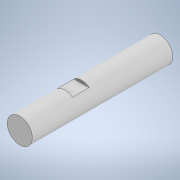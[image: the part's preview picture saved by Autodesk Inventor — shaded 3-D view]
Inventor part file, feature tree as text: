
AUTODESK INVENTOR PART (.ipt)
format: ipt  version: 2021 (Build 250183000, 183)  size: 99,840 bytes
history: native  units: in
note: dims shown in document units (in); Inventor stores cm internally (conversion verified against a paired STEP export)
features: extrude x2, sketch x2, other x1, plane x1
ambient origin geometry x8: Origin, YZ Plane, XZ Plane, XY Plane, X Axis, Y Axis, Z Axis, Center Point
bodies: Body1 (feature_tree)
feature tree (6):
  other  "Sólido1"
  extrude  "Extrusión1"  Depth=3.3071in TaperAngle=0.0deg
  plane  "Plano de trabajo1"
  extrude  "Extrusión2"  Depth=0.3937in
  sketch  "Boceto1"  dims[d0=0.5906in d1=3.3071in d2=0.0in]
  sketch  "Boceto3"  dims[d3=0.1969in d4=0.0591in d5=0.3937in d6=0.0in]
